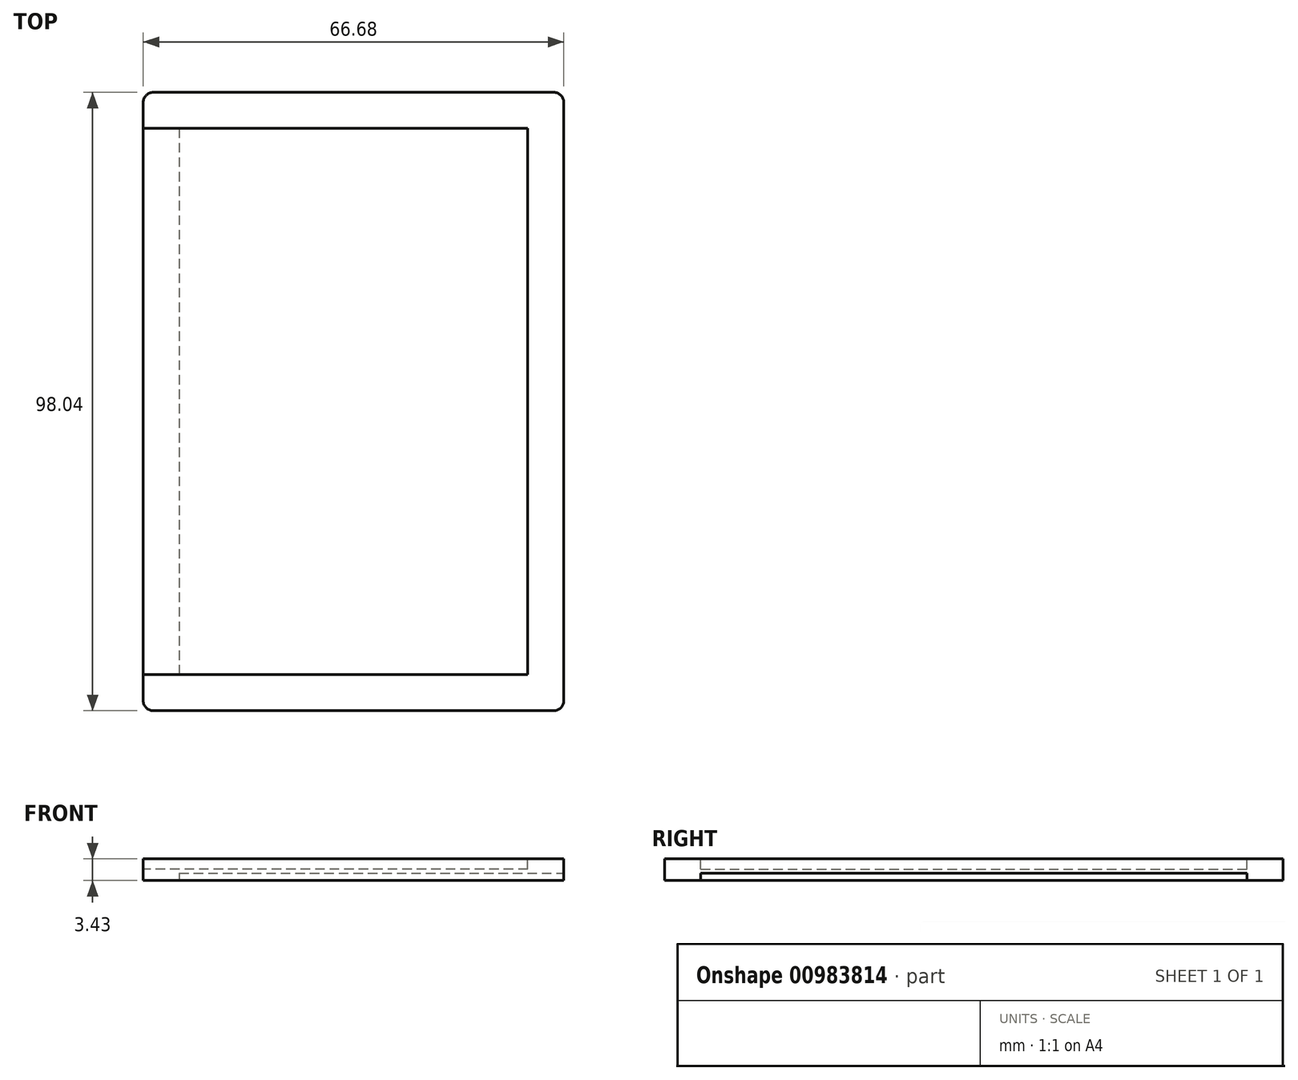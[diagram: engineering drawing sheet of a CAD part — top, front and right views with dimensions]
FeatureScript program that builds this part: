
annotation { "Feature Type Name" : "Feature", "Feature Type Description" : "" }
export const myFeature = defineFeature(function(context is Context, id is Id, definition is map)
    precondition{}
    {
        {
            var Q0;
            Q0=qCreatedBy(makeId("Top.planeOp"),FACE);
            var sketch = newSketch(context, id + "F0", { "sketchPlane" : qUnion([Q0])});
            skLineSegment(sketch, "E0.bottom", {"start": v(31.75, -49.02) * mm, "end": v(-31.75, -49.02) * mm});
            skLineSegment(sketch, "E0.top", {"start": v(31.75, 49.02) * mm, "end": v(-31.75, 49.02) * mm});
            skLineSegment(sketch, "E0.left", {"start": v(33.34, -47.43) * mm, "end": v(33.34, 47.43) * mm});
            skLineSegment(sketch, "E0.right", {"start": v(-33.34, -47.43) * mm, "end": v(-33.34, 47.43) * mm});
            skPoint(sketch, "E0.middle", {"position": v(0, 0) * mm});
            skPoint(sketch, "E1.visualSharp", {"position": v(-33.34, 49.02) * mm});
            skArc(sketch, "E1.filletArc", {"start": v(-31.75, 49.02) * mm, "mid": v(-32.87, 48.56) * mm, "end": v(-33.34, 47.43) * mm});
            skPoint(sketch, "E2.visualSharp", {"position": v(33.34, 49.02) * mm});
            skArc(sketch, "E2.filletArc", {"start": v(33.34, 47.43) * mm, "mid": v(32.87, 48.56) * mm, "end": v(31.75, 49.02) * mm});
            skPoint(sketch, "E3.visualSharp", {"position": v(33.34, -49.02) * mm});
            skArc(sketch, "E3.filletArc", {"start": v(31.75, -49.02) * mm, "mid": v(32.87, -48.56) * mm, "end": v(33.34, -47.43) * mm});
            skPoint(sketch, "E4.visualSharp", {"position": v(-33.34, -49.02) * mm});
            skArc(sketch, "E4.filletArc", {"start": v(-33.34, -47.43) * mm, "mid": v(-32.87, -48.56) * mm, "end": v(-31.75, -49.02) * mm});
            skSolve(sketch);
        }
        {
            var Q0;
            Q0 = qSketchRegion(id + "F0", true);
            extrude(context, id + "F1", {"entities" : qUnion([Q0]), "depth" : 3.43 * mm, "offsetDistance" : 25.4 * mm});
        }
        {
            var Q0;
            Q0=makeQuery(id+"F1.opExtrude","CAP_FACE",FACE,{"disambiguationData":[OSD([sQuery(id+"F0.wireOp",EDGE,"E0.bottom"),sQuery(id+"F0.wireOp",EDGE,"E0.top"),sQuery(id+"F0.wireOp",EDGE,"E0.left"),sQuery(id+"F0.wireOp",EDGE,"E0.right"),sQuery(id+"F0.wireOp",EDGE,"E1.filletArc"),sQuery(id+"F0.wireOp",EDGE,"E2.filletArc"),sQuery(id+"F0.wireOp",EDGE,"E3.filletArc"),sQuery(id+"F0.wireOp",EDGE,"E4.filletArc")])],"isStart":false});
            var sketch = newSketch(context, id + "F2", { "sketchPlane" : qUnion([Q0])});
            skLineSegment(sketch, "E5.bottom", {"start": v(27.62, -43.3) * mm, "end": v(-27.62, -43.3) * mm});
            skLineSegment(sketch, "E5.top", {"start": v(27.62, 43.3) * mm, "end": v(-27.62, 43.3) * mm});
            skLineSegment(sketch, "E5.left", {"start": v(27.62, -43.3) * mm, "end": v(27.62, 43.3) * mm});
            skPoint(sketch, "E5.middle", {"position": v(0, 0) * mm});
            skLineSegment(sketch, "E6", {"start": v(-27.62, 43.3) * mm, "end": v(-33.34, 43.3) * mm});
            skLineSegment(sketch, "E7", {"start": v(-27.62, -43.3) * mm, "end": v(-33.34, -43.3) * mm});
            skLineSegment(sketch, "E8", {"start": v(-33.34, 43.3) * mm, "end": v(-33.34, -43.3) * mm});
            skSolve(sketch);
        }
        {
            var Q0;
            Q0=makeQuery(id+"F2.imprint","IMPRINT",FACE,{"disambiguationData":[TD([[makeQuery(id+"F2.imprint","IMPRINT",EDGE,{"derivedFrom":sQuery(id+"F2.wireOp",EDGE,"E5.bottom")}),-1.0]])]});
            extrude(context, id + "F3", {"entities" : qUnion([Q0]), "operationType" : NewBodyOperationType.REMOVE, "oppositeDirection" : true, "depth" : 1.65 * mm, "offsetDistance" : 25.4 * mm});
        }
        {
            var Q0;
            Q0=makeQuery(id+"F1.opExtrude","CAP_FACE",FACE,{"disambiguationData":[OSD([sQuery(id+"F0.wireOp",EDGE,"E0.bottom"),sQuery(id+"F0.wireOp",EDGE,"E0.top"),sQuery(id+"F0.wireOp",EDGE,"E0.left"),sQuery(id+"F0.wireOp",EDGE,"E0.right"),sQuery(id+"F0.wireOp",EDGE,"E1.filletArc"),sQuery(id+"F0.wireOp",EDGE,"E2.filletArc"),sQuery(id+"F0.wireOp",EDGE,"E3.filletArc"),sQuery(id+"F0.wireOp",EDGE,"E4.filletArc")])],"isStart":true});
            var sketch = newSketch(context, id + "F4", { "sketchPlane" : qUnion([Q0])});
            skLineSegment(sketch, "E9.bottom", {"start": v(27.62, -43.3) * mm, "end": v(-27.62, -43.3) * mm});
            skLineSegment(sketch, "E9.top", {"start": v(27.62, 43.3) * mm, "end": v(-27.62, 43.3) * mm});
            skLineSegment(sketch, "E9.right", {"start": v(-27.62, -43.3) * mm, "end": v(-27.62, 43.3) * mm});
            skPoint(sketch, "E9.middle", {"position": v(0, 0) * mm});
            skLineSegment(sketch, "E10", {"start": v(27.62, 43.3) * mm, "end": v(33.34, 43.3) * mm});
            skLineSegment(sketch, "E11", {"start": v(27.62, -43.3) * mm, "end": v(33.34, -43.3) * mm});
            skSolve(sketch);
        }
        {
            var Q0;
            Q0=makeQuery(id+"F4.imprint","IMPRINT",FACE,{"disambiguationData":[TD([[makeQuery(id+"F4.imprint","IMPRINT",EDGE,{"derivedFrom":sQuery(id+"F4.wireOp",EDGE,"E9.bottom")}),-1.0]])]});
            extrude(context, id + "F5", {"entities" : qUnion([Q0]), "operationType" : NewBodyOperationType.REMOVE, "oppositeDirection" : true, "depth" : 1.14 * mm, "offsetDistance" : 25.4 * mm});
        }
    });
